# Revit family: AFX-Glo-Linear_Semi_Flush-1
name_source: partatom
category: Lighting Fixtures
units: mm (PartAtom-declared; Revit-internal decimal feet)

## family parameters
Cut with Voids When Loaded = No
Host = Face
Light Source = Yes
Part Type = Normal
Room Calculation Point = No
Round Connector Dimension = Use Diameter
Shared = No

## types (1)
- GLOL4812L30D1BK
    Apparent Load = 120 VA
    Assembly Code = D5020200
    Body Finish = AFX - Aluminum Black
    Cable Finish = AFX - Aluminum Black
    Canopy Finish = AFX - Aluminum Black
    Color Filter = 16777215
    Color Rendering Index = 90
    Colour Rendering Index = 90 CRI
    Connector Finish = AFX - Aluminum Black
    Default Elevation = 48"
    Depth = 11 3/4"
    Description = LED Linear Semi-Flush - 47 1/4"L x 11 3/4"W x 2"D
    Diffuser Finish = AFX - White Acrylic
    Dimming Lamp Color Temperature Shift = <None>
    Emit Shape Visible in Rendering = No
    Emit from Rectangle Length = 48"
    Emit from Rectangle Width = 24"
    Height = 1 1/4"
    Lamp = LED
    Length = 47 1/4"
    Manufacturer = AFX Inc
    Model = GLOL4812L30D1BK
    Photometric Web File = GLOL4812L30D1xx_IES.IES
    Product Documentation Link = https://www.afxinc.com
    Revit Model Built By = https://servex-us.com
    Tilt Angle = 90.00°
    Type Comments = GLO
    URL = https://www.afxinc.com
    Voltage = 120 V
    Wattage Comments = 40W

## geometry (parser evidence)
native form markers: Sweep x4
no freeform markers — native parametric forms only
